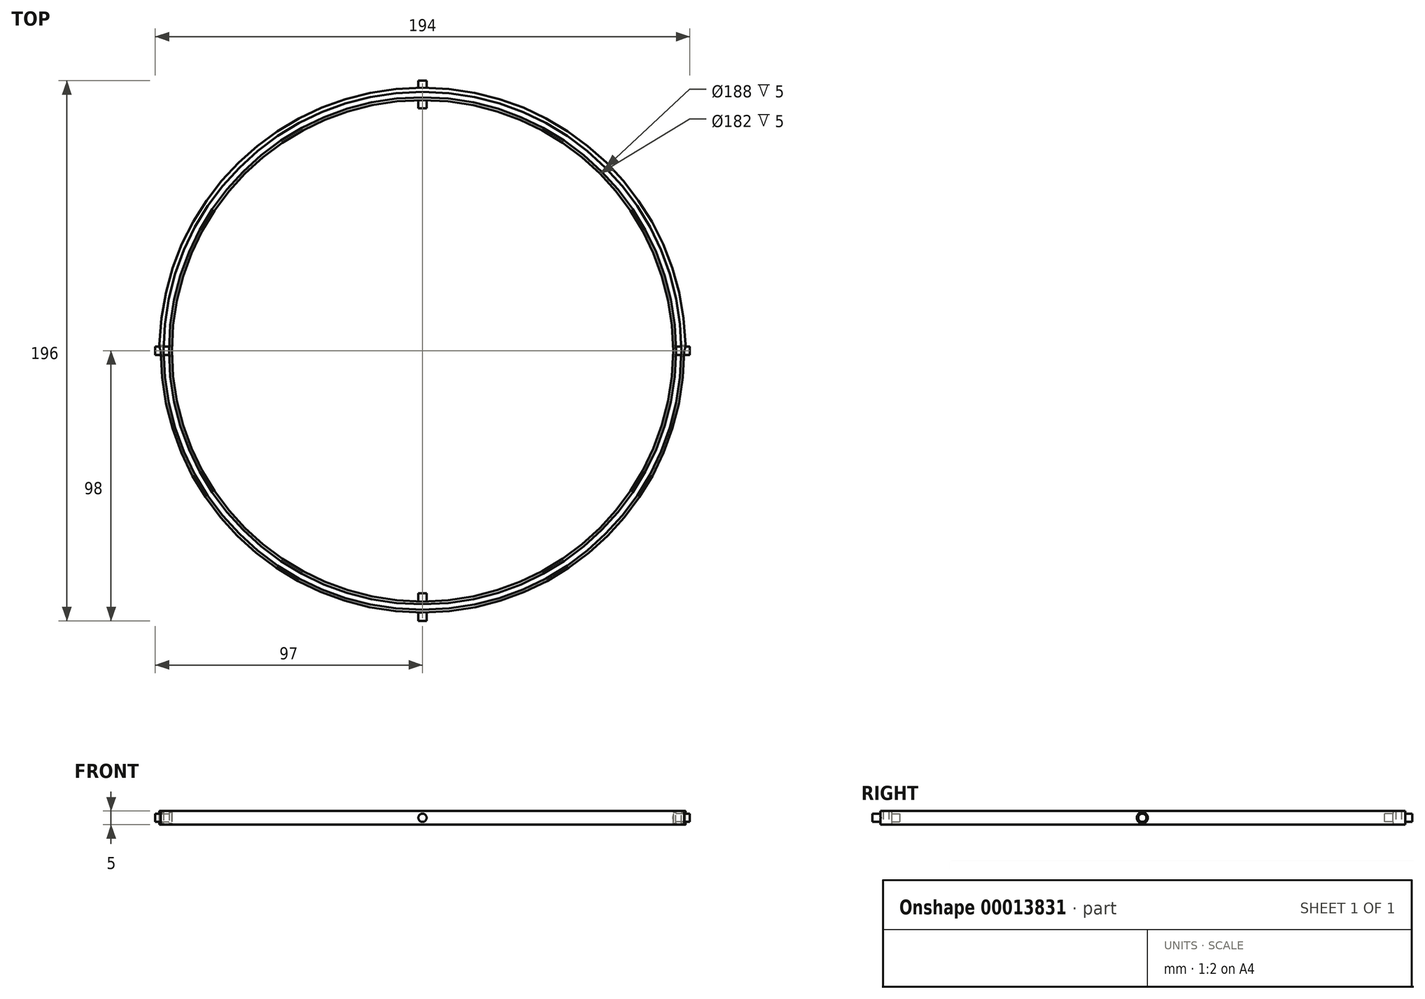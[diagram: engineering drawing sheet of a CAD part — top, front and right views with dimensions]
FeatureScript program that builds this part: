
annotation { "Feature Type Name" : "Feature", "Feature Type Description" : "" }
export const myFeature = defineFeature(function(context is Context, id is Id, definition is map)
    precondition{}
    {
        {
            var Q0;
            Q0=qCreatedBy(makeId("Top.planeOp"),FACE);
            var sketch = newSketch(context, id + "F0", { "sketchPlane" : qUnion([Q0])});
            skCircle(sketch, "E0", {"center": v(0, 0) * mm, "radius": 91 * mm});
            skCircle(sketch, "E1", {"center": v(0, 0) * mm, "radius": 92 * mm});
            skLineSegment(sketch, "E2", {"start": v(0, 91) * mm, "end": v(0, 92) * mm, "construction": true});
            skCircle(sketch, "E3", {"center": v(0, 0) * mm, "radius": 94 * mm});
            skCircle(sketch, "E4", {"center": v(0, 0) * mm, "radius": 95 * mm});
            skLineSegment(sketch, "E5", {"start": v(0, 94) * mm, "end": v(0, 95) * mm, "construction": true});
            skCircle(sketch, "E6", {"center": v(0, 0) * mm, "radius": 95.5 * mm});
            skLineSegment(sketch, "E7", {"start": v(0, 95) * mm, "end": v(0, 95.5) * mm, "construction": true});
            skLineSegment(sketch, "E8", {"start": v(-95.5, 0) * mm, "end": v(95.5, 0) * mm});
            skSolve(sketch);
        }
        {
            var Q0;
            Q0=qCreatedBy(makeId("Front.planeOp"),FACE);
            var sketch = newSketch(context, id + "F1", { "sketchPlane" : qUnion([Q0])});
            skCircle(sketch, "E9", {"center": v(0, 0) * mm, "radius": 1.5 * mm});
            skCircle(sketch, "E10", {"center": v(0, 0) * mm, "radius": 2 * mm});
            skLineSegment(sketch, "E11", {"start": v(0, 1.5) * mm, "end": v(0, 2) * mm, "construction": true});
            skSolve(sketch);
        }
        {
            var Q0;
            Q0=qCreatedBy(makeId("Right.planeOp"),FACE);
            var sketch = newSketch(context, id + "F2", { "sketchPlane" : qUnion([Q0])});
            skCircle(sketch, "E12", {"center": v(0, 0) * mm, "radius": 1.5 * mm});
            skCircle(sketch, "E13", {"center": v(0, 0) * mm, "radius": 2 * mm});
            skLineSegment(sketch, "E14", {"start": v(0, 1.5) * mm, "end": v(0, 2) * mm, "construction": true});
            skSolve(sketch);
        }
        {
            var Q0;
            Q0=makeQuery(id+"F0.imprint","IMPRINT",FACE,{"disambiguationData":[TD([[makeQuery(id+"F0.imprint","IMPRINT",EDGE,{"derivedFrom":sQuery(id+"F0.wireOp",EDGE,"E0")}),-1.0]])]});
            extrude(context, id + "F3", {"entities" : qUnion([Q0]), "endBound" : BoundingType.SYMMETRIC, "depth" : 5 * mm});
        }
        {
            var Q0;
            Q0=makeQuery(id+"F0.imprint","IMPRINT",FACE,{"disambiguationData":[TD([[makeQuery(id+"F0.imprint","IMPRINT",EDGE,{"derivedFrom":sQuery(id+"F0.wireOp",EDGE,"E3")}),-1.0]])]});
            var Q1;
            {var subQ0=sQuery(id+"F0.wireOp",EDGE,"E8");var subQ1=sQuery(id+"F0.wireOp",EDGE,"E4");var subQ5=makeQuery(id+"F0.imprint","INTERSECT",VERTEX,{"disambiguationData":[OD(0.0)],"derivedFrom":[subQ1,subQ0]});Q1=makeQuery(id+"F0.imprint","IMPRINT",FACE,{"disambiguationData":[TD([[makeQuery(id+"F0.imprint","IMPRINT",EDGE,{"disambiguationData":[TD([[subQ5,-1.0]])],"derivedFrom":subQ1}),-1.0]])]});}
            extrude(context, id + "F4", {"entities" : qUnion([Q0, Q1]), "endBound" : BoundingType.SYMMETRIC, "depth" : 5 * mm});
        }
        {
            var Q0;
            Q0=makeQuery(id+"F2.imprint","IMPRINT",FACE,{"disambiguationData":[TD([[makeQuery(id+"F2.imprint","IMPRINT",EDGE,{"derivedFrom":sQuery(id+"F2.wireOp",EDGE,"E12")}),1.0]])]});
            var Q1;
            Q1=makeQuery(id+"F2.imprint","IMPRINT",FACE,{"disambiguationData":[TD([[makeQuery(id+"F2.imprint","IMPRINT",EDGE,{"derivedFrom":sQuery(id+"F2.wireOp",EDGE,"E12")}),-1.0]])]});
            extrude(context, id + "F5", {"entities" : qUnion([Q0, Q1]), "operationType" : NewBodyOperationType.REMOVE, "endBound" : BoundingType.THROUGH_ALL, "oppositeDirection" : true, "depth" : 25 * mm, "hasSecondDirection" : true, "secondDirectionBound" : SecondDirectionBoundingType.THROUGH_ALL, "secondDirectionOppositeDirection" : false, "secondDirectionDepth" : 25 * mm});
        }
        {
            var Q0;
            Q0=makeQuery(id+"F2.imprint","IMPRINT",FACE,{"disambiguationData":[TD([[makeQuery(id+"F2.imprint","IMPRINT",EDGE,{"derivedFrom":sQuery(id+"F2.wireOp",EDGE,"E12")}),1.0]])]});
            var Q1;
            Q1=makeQuery(id+"F3.opExtrude","SWEPT_FACE",FACE,{"disambiguationData":[OSD([sQuery(id+"F0.wireOp",EDGE,"E1")])]});
            var Q2;
            Q2=makeQuery(id+"F3.opExtrude","SWEPT_FACE",FACE,{"disambiguationData":[OSD([sQuery(id+"F0.wireOp",EDGE,"E0")])]});
            extrude(context, id + "F6", {"entities" : qUnion([Q0]), "operationType" : NewBodyOperationType.ADD, "endBoundEntity" : qUnion([Q1]), "depth" : 97 * mm, "hasSecondDirection" : true, "secondDirectionBound" : SecondDirectionBoundingType.UP_TO_SURFACE, "secondDirectionOppositeDirection" : false, "secondDirectionBoundEntityFace" : qUnion([Q2]), "secondDirectionDepth" : 25 * mm});
        }
        {
            var Q0;
            Q0=makeQuery(id+"F2.imprint","IMPRINT",FACE,{"disambiguationData":[TD([[makeQuery(id+"F2.imprint","IMPRINT",EDGE,{"derivedFrom":sQuery(id+"F2.wireOp",EDGE,"E12")}),1.0]])]});
            var Q1;
            Q1=makeQuery(id+"F3.opExtrude","SWEPT_FACE",FACE,{"disambiguationData":[OSD([sQuery(id+"F0.wireOp",EDGE,"E0")])]});
            extrude(context, id + "F7", {"entities" : qUnion([Q0]), "operationType" : NewBodyOperationType.ADD, "oppositeDirection" : true, "depth" : 97 * mm, "hasSecondDirection" : true, "secondDirectionBound" : SecondDirectionBoundingType.UP_TO_SURFACE, "secondDirectionOppositeDirection" : true, "secondDirectionBoundEntityFace" : qUnion([Q1]), "secondDirectionDepth" : 25 * mm});
        }
        {
            var Q0;
            Q0=makeQuery(id+"F1.imprint","IMPRINT",FACE,{"disambiguationData":[TD([[makeQuery(id+"F1.imprint","IMPRINT",EDGE,{"derivedFrom":sQuery(id+"F1.wireOp",EDGE,"E9")}),1.0]])]});
            var Q1;
            Q1=makeQuery(id+"F3.opExtrude","SWEPT_FACE",FACE,{"disambiguationData":[OSD([sQuery(id+"F0.wireOp",EDGE,"E0")])]});
            extrude(context, id + "F8", {"entities" : qUnion([Q0]), "operationType" : NewBodyOperationType.ADD, "endBound" : BoundingType.UP_TO_SURFACE, "endBoundEntityFace" : qUnion([Q1]), "depth" : 25 * mm, "hasSecondDirection" : true, "secondDirectionOppositeDirection" : false, "secondDirectionDepth" : 88 * mm});
        }
        {
            var Q0;
            Q0=makeQuery(id+"F1.imprint","IMPRINT",FACE,{"disambiguationData":[TD([[makeQuery(id+"F1.imprint","IMPRINT",EDGE,{"derivedFrom":sQuery(id+"F1.wireOp",EDGE,"E9")}),1.0]])]});
            var Q1;
            Q1=makeQuery(id+"F3.opExtrude","SWEPT_FACE",FACE,{"disambiguationData":[OSD([sQuery(id+"F0.wireOp",EDGE,"E0")])]});
            extrude(context, id + "F9", {"entities" : qUnion([Q0]), "operationType" : NewBodyOperationType.ADD, "endBound" : BoundingType.UP_TO_SURFACE, "oppositeDirection" : true, "endBoundEntityFace" : qUnion([Q1]), "depth" : 25 * mm, "hasSecondDirection" : true, "secondDirectionOppositeDirection" : true, "secondDirectionDepth" : 88 * mm});
        }
        {
            var Q0;
            Q0=makeQuery(id+"F1.imprint","IMPRINT",FACE,{"disambiguationData":[TD([[makeQuery(id+"F1.imprint","IMPRINT",EDGE,{"derivedFrom":sQuery(id+"F1.wireOp",EDGE,"E9")}),1.0]])]});
            var Q1;
            Q1=makeQuery(id+"F4.opExtrude","SWEPT_FACE",FACE,{"disambiguationData":[OSD([sQuery(id+"F0.wireOp",EDGE,"E3")])]});
            extrude(context, id + "F10", {"entities" : qUnion([Q0]), "operationType" : NewBodyOperationType.ADD, "depth" : 98 * mm, "hasSecondDirection" : true, "secondDirectionBound" : SecondDirectionBoundingType.UP_TO_SURFACE, "secondDirectionOppositeDirection" : false, "secondDirectionBoundEntityFace" : qUnion([Q1]), "secondDirectionDepth" : 25 * mm});
        }
        {
            var Q0;
            Q0=makeQuery(id+"F1.imprint","IMPRINT",FACE,{"disambiguationData":[TD([[makeQuery(id+"F1.imprint","IMPRINT",EDGE,{"derivedFrom":sQuery(id+"F1.wireOp",EDGE,"E9")}),1.0]])]});
            var Q1;
            Q1=makeQuery(id+"F4.opExtrude","SWEPT_FACE",FACE,{"disambiguationData":[OSD([sQuery(id+"F0.wireOp",EDGE,"E3")])]});
            extrude(context, id + "F11", {"entities" : qUnion([Q0]), "operationType" : NewBodyOperationType.ADD, "oppositeDirection" : true, "depth" : 98 * mm, "hasSecondDirection" : true, "secondDirectionBound" : SecondDirectionBoundingType.UP_TO_SURFACE, "secondDirectionOppositeDirection" : true, "secondDirectionBoundEntityFace" : qUnion([Q1]), "secondDirectionDepth" : 25 * mm});
        }
        {
            var Q0;
            {var subQ0=sQuery(id+"F0.wireOp",EDGE,"E8");var subQ1=sQuery(id+"F0.wireOp",EDGE,"E6");var subQ2=sQuery(id+"F0.wireOp",EDGE,"E4");var subQ3=makeQuery(id+"F0.imprint","INTERSECT",VERTEX,{"disambiguationData":[OD(1.0)],"derivedFrom":[subQ1,subQ0]});Q0=makeQuery(id+"F5.boolean.opBoolean","SPLIT",EDGE,{"disambiguationData":[TD([makeQuery(id+"F4.opExtrude","CAP_FACE",FACE,{"disambiguationData":[OSD([sQuery(id+"F0.wireOp",EDGE,"E3"),subQ2,subQ1,subQ0])],"isStart":false})])],"derivedFrom":makeQuery(id+"F4.opExtrude","SWEPT_EDGE",EDGE,{"disambiguationData":[OSD([subQ1,subQ0]),TDD([subQ3])]})});}
            var Q1;
            {var subQ0=sQuery(id+"F0.wireOp",EDGE,"E8");var subQ1=sQuery(id+"F0.wireOp",EDGE,"E6");var subQ2=sQuery(id+"F0.wireOp",EDGE,"E4");var subQ3=makeQuery(id+"F0.imprint","INTERSECT",VERTEX,{"disambiguationData":[OD(0.0)],"derivedFrom":[subQ1,subQ0]});Q1=makeQuery(id+"F5.boolean.opBoolean","SPLIT",EDGE,{"disambiguationData":[TD([makeQuery(id+"F4.opExtrude","CAP_FACE",FACE,{"disambiguationData":[OSD([sQuery(id+"F0.wireOp",EDGE,"E3"),subQ2,subQ1,subQ0])],"isStart":false})])],"derivedFrom":makeQuery(id+"F4.opExtrude","SWEPT_EDGE",EDGE,{"disambiguationData":[OSD([subQ1,subQ0]),TDD([subQ3])]})});}
            fillet(context, id + "F12", {"entities" : qUnion([Q0, Q1]), "radius" : 5 * mm, "tangentPropagation" : true, "allowEdgeOverflow" : false});
        }
    });
